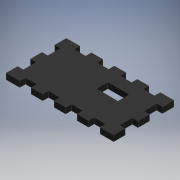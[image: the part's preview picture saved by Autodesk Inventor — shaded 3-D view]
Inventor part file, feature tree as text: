
AUTODESK INVENTOR PART (.ipt)
format: ipt  version: 2019 (Build 230136000, 136)  size: 179,712 bytes
history: native  units: mm
features: extrude x2, sketch x2
ambient origin geometry x8: Origin, YZ Plane, XZ Plane, XY Plane, X Axis, Y Axis, Z Axis, Center Point
bodies: Solid1 (feature_tree)
feature tree (4):
  extrude  "Extrusion1"  Depth=42.0mm
  extrude  "Extrusion2"  Depth=4.0mm
  sketch  "Sketch1"  dims[d0=75.0mm d1=42.0mm]
  sketch  "Sketch2"  dims[d10=4.0mm d11=0.0mm d12=4.0mm d13=4.0mm d14=8.0mm d15=8.0mm d16=8.0mm d17=8.0mm d18=4.0mm d19=4.0mm d20=0.0mm d21=15.0mm d22=19.0mm d23=8.0mm d24=22.0mm]
